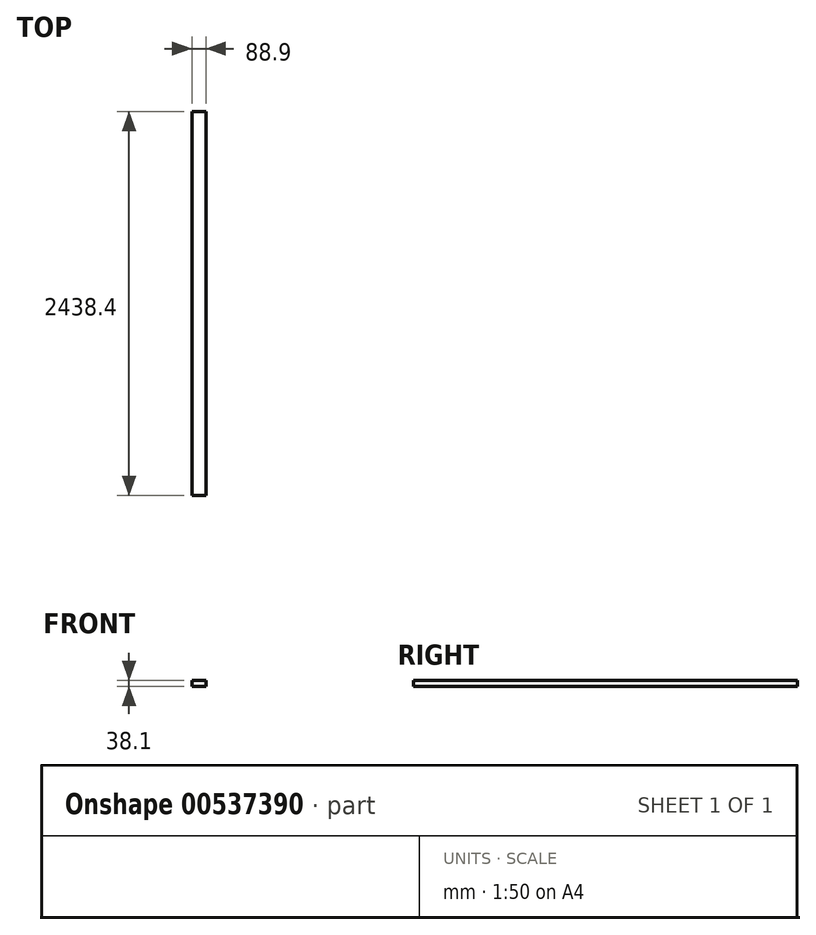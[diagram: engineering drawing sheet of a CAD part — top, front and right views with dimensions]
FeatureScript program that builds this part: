
annotation { "Feature Type Name" : "Feature", "Feature Type Description" : "" }
export const myFeature = defineFeature(function(context is Context, id is Id, definition is map)
    precondition{}
    {
        {
            var Q0;
            Q0=qCreatedBy(makeId("Front.planeOp"),FACE);
            var sketch = newSketch(context, id + "F0", { "sketchPlane" : qUnion([Q0])});
            skLineSegment(sketch, "E0.bottom", {"start": v(44.45, 19.05) * mm, "end": v(-44.45, 19.05) * mm});
            skLineSegment(sketch, "E0.top", {"start": v(44.45, -19.05) * mm, "end": v(-44.45, -19.05) * mm});
            skLineSegment(sketch, "E0.left", {"start": v(44.45, 19.05) * mm, "end": v(44.45, -19.05) * mm});
            skLineSegment(sketch, "E0.right", {"start": v(-44.45, 19.05) * mm, "end": v(-44.45, -19.05) * mm});
            skPoint(sketch, "E0.middle", {"position": v(0, 0) * mm});
            skSolve(sketch);
        }
        {
            var Q0;
            Q0=makeQuery(id+"F0.imprint","IMPRINT",FACE,{"disambiguationData":[TD([[makeQuery(id+"F0.imprint","IMPRINT",EDGE,{"derivedFrom":sQuery(id+"F0.wireOp",EDGE,"E0.bottom")}),1.0]])]});
            extrude(context, id + "F1", {"entities" : qUnion([Q0]), "endBound" : BoundingType.SYMMETRIC, "depth" : 2438.4 * mm, "offsetDistance" : 25 * mm});
        }
    });
